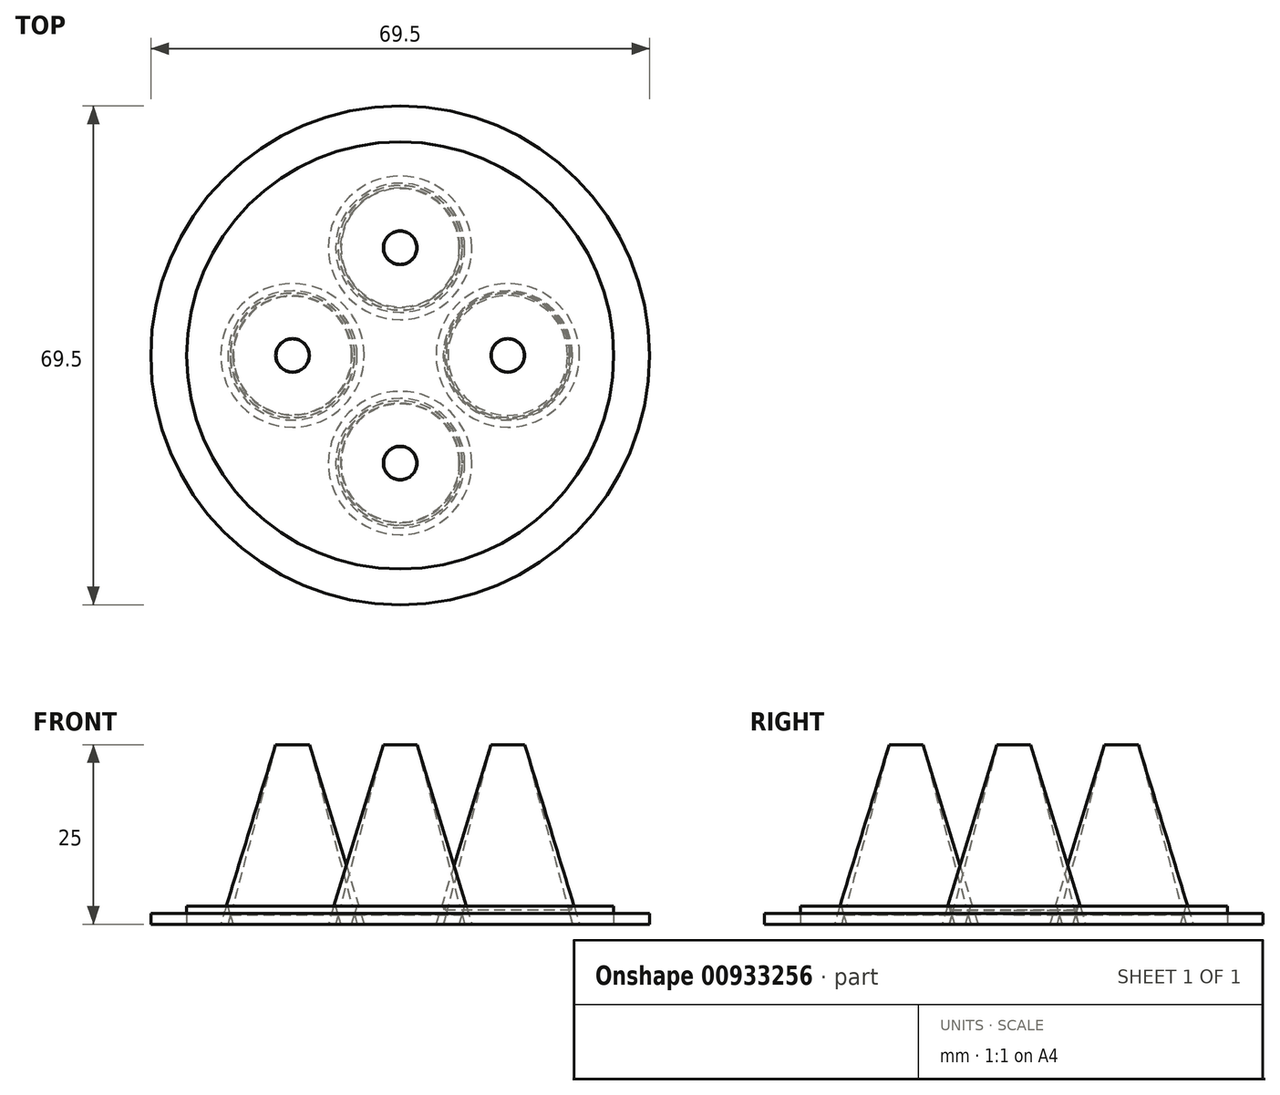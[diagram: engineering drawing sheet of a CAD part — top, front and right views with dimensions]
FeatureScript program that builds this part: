
annotation { "Feature Type Name" : "Feature", "Feature Type Description" : "" }
export const myFeature = defineFeature(function(context is Context, id is Id, definition is map)
    precondition{}
    {
        {
            var Q0;
            Q0=qCreatedBy(makeId("Top.planeOp"),FACE);
            var sketch = newSketch(context, id + "F0", { "sketchPlane" : qUnion([Q0])});
            skCircle(sketch, "E0", {"center": v(0, 0) * mm, "radius": 34.75 * mm});
            skSolve(sketch);
        }
        {
            var Q0;
            Q0=qCreatedBy(makeId("Top.planeOp"),FACE);
            var sketch = newSketch(context, id + "F1", { "sketchPlane" : qUnion([Q0])});
            skLineSegment(sketch, "E1", {"start": v(0, 0) * mm, "end": v(15, 0) * mm, "construction": true});
            skCircle(sketch, "E2", {"center": v(15, 0) * mm, "radius": 10 * mm});
            skSolve(sketch);
        }
        {
            var Q0;
            Q0=qCreatedBy(makeId("Top.planeOp"),FACE);
            var sketch = newSketch(context, id + "F2", { "sketchPlane" : qUnion([Q0])});
            skCircle(sketch, "E3", {"center": v(0, 0) * mm, "radius": 29.75 * mm});
            skSolve(sketch);
        }
        {
            var Q0;
            Q0=makeQuery(id+"F1.imprint","IMPRINT",FACE,{"disambiguationData":[TD([[makeQuery(id+"F1.imprint","IMPRINT",EDGE,{"derivedFrom":sQuery(id+"F1.wireOp",EDGE,"E2")}),1.0]])]});
            extrude(context, id + "F3", {"entities" : qUnion([Q0]), "depth" : 25 * mm, "offsetDistance" : 25 * mm, "hasDraft" : true, "draftAngle" : 17 * degree, "draftPullDirection" : true});
        }
        {
            var Q0;
            Q0=qCreatedBy(makeId("Top.planeOp"),FACE);
            var sketch = newSketch(context, id + "F4", { "sketchPlane" : qUnion([Q0])});
            skCircle(sketch, "E4", {"center": v(15, 0) * mm, "radius": 9 * mm});
            skSolve(sketch);
        }
        {
            var Q0;
            Q0 = qSketchRegion(id + "F2", true);
            extrude(context, id + "F5", {"entities" : qUnion([Q0]), "depth" : 2.5 * mm, "offsetDistance" : 25 * mm});
        }
        {
            var Q0;
            Q0=makeQuery(id+"F0.imprint","IMPRINT",FACE,{"disambiguationData":[TD([[makeQuery(id+"F0.imprint","IMPRINT",EDGE,{"derivedFrom":sQuery(id+"F0.wireOp",EDGE,"E0")}),1.0]])]});
            extrude(context, id + "F6", {"entities" : qUnion([Q0]), "depth" : 1.5 * mm, "offsetDistance" : 25 * mm});
        }
        {
            var Q0;
            Q0=makeQuery(id+"F4.imprint","IMPRINT",FACE,{"disambiguationData":[TD([[makeQuery(id+"F4.imprint","IMPRINT",EDGE,{"derivedFrom":sQuery(id+"F4.wireOp",EDGE,"E4")}),1.0]])]});
            var Q1;
            Q1 = qSketchRegion(id + "F9", true);
            extrude(context, id + "F7", {"entities" : qUnion([Q0, Q1]), "operationType" : NewBodyOperationType.REMOVE, "endBound" : BoundingType.THROUGH_ALL, "depth" : 25 * mm, "offsetDistance" : 25 * mm, "hasDraft" : true, "draftAngle" : 15 * degree, "draftPullDirection" : true});
        }
        {
            var Q0;
            Q0=makeQuery(id+"F3.opExtrude","SWEPT_BODY",BODY,{"disambiguationData":[OSD([sQuery(id+"F1.wireOp",EDGE,"E2")])]});
            var Q1;
            Q1=sQuery(id+"F0.wireOp",EDGE,"E0");
            circularPattern(context, id + "F8", {"entities" : qUnion([Q0]), "axis" : qUnion([Q1]), "angle" : 360 * degree, "instanceCount" : 4, "equalSpace" : true});
        }
        {
            var Q0;
            Q0=makeQuery(id+"F5.opExtrude","CAP_FACE",FACE,{"disambiguationData":[OSD([sQuery(id+"F2.wireOp",EDGE,"E3")])],"isStart":false});
            var sketch = newSketch(context, id + "F9", { "sketchPlane" : qUnion([Q0])});
            skCircle(sketch, "E5.0", {"center": v(0, -15) * mm, "radius": 9 * mm});
            skCircle(sketch, "E6.0", {"center": v(15, 0) * mm, "radius": 9 * mm});
            skCircle(sketch, "E7.0", {"center": v(0, 15) * mm, "radius": 9 * mm});
            skCircle(sketch, "E8.0", {"center": v(-15, 0) * mm, "radius": 9 * mm});
            skCircle(sketch, "E9", {"center": v(15, 0) * mm, "radius": 8.65 * mm});
            skSolve(sketch);
        }
        {
            var Q0;
            Q0 = qSketchRegion(id + "F9", true);
            extrude(context, id + "F10", {"entities" : qUnion([Q0]), "operationType" : NewBodyOperationType.REMOVE, "oppositeDirection" : true, "depth" : 2.5 * mm, "offsetDistance" : 25 * mm, "hasDraft" : true, "draftAngle" : 17 * degree, "draftPullDirection" : true});
        }
    });
